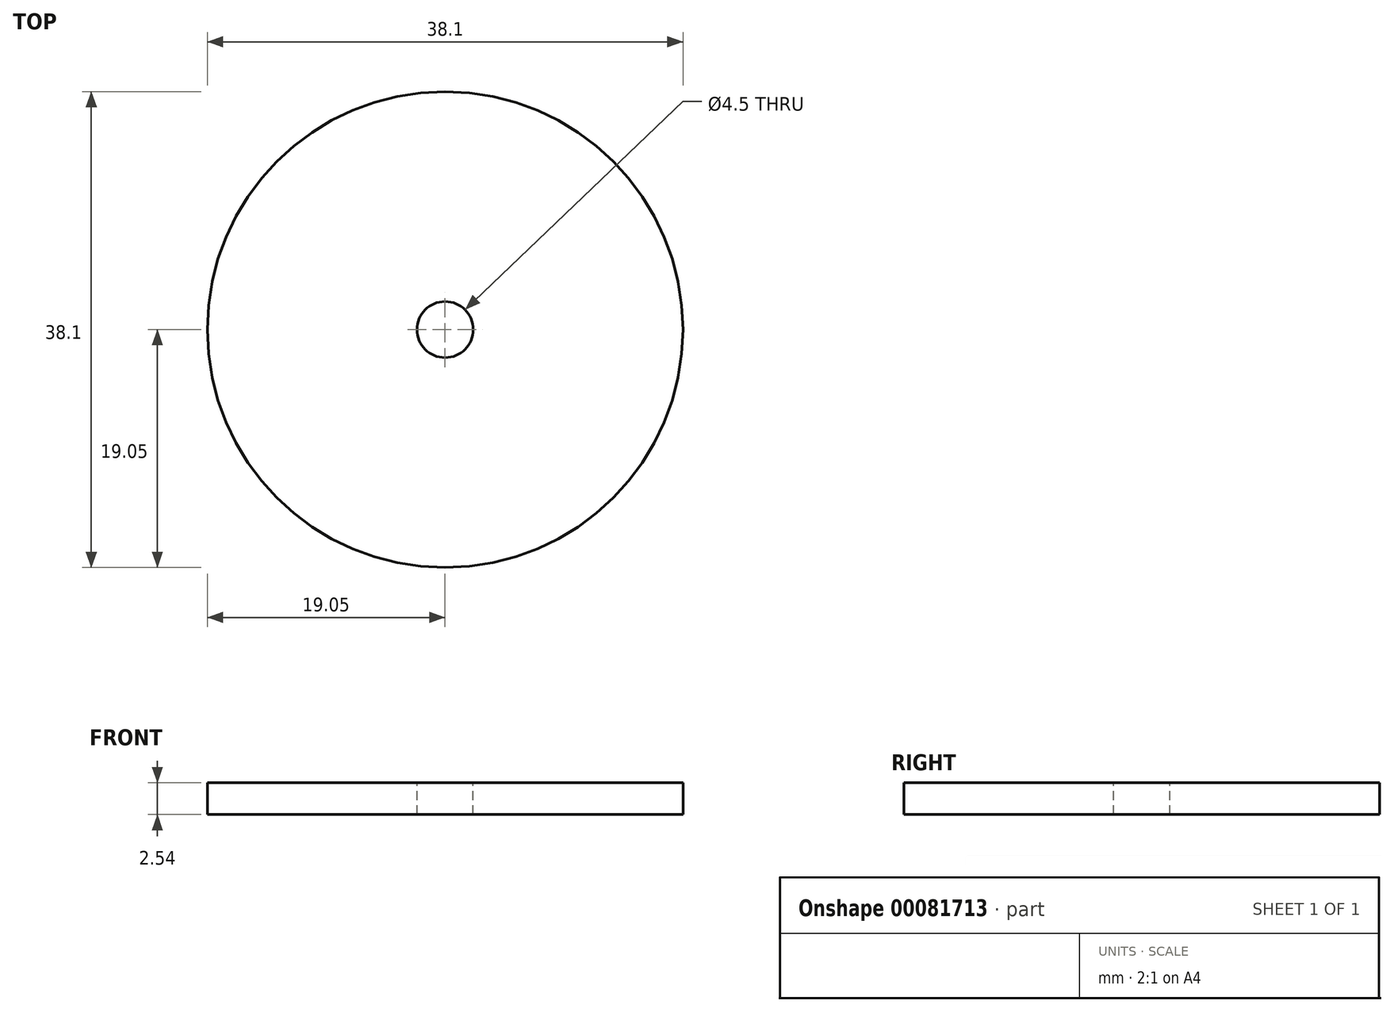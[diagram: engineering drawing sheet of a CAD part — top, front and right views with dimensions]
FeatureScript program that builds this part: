
annotation { "Feature Type Name" : "Feature", "Feature Type Description" : "" }
export const myFeature = defineFeature(function(context is Context, id is Id, definition is map)
    precondition{}
    {
        {
            var Q0;
            Q0=qCreatedBy(makeId("Top.planeOp"),FACE);
            var sketch = newSketch(context, id + "F0", { "sketchPlane" : qUnion([Q0])});
            skCircle(sketch, "E0", {"center": v(0, 0) * mm, "radius": 19.05 * mm});
            skSolve(sketch);
        }
        {
            var Q0;
            Q0 = qSketchRegion(id + "F0", true);
            extrude(context, id + "F1", {"entities" : qUnion([Q0]), "depth" : 2.54 * mm});
        }
        {
            var Q0;
            Q0=makeQuery(id+"F1.opExtrude","CAP_FACE",FACE,{"disambiguationData":[OSD([sQuery(id+"F0.wireOp",EDGE,"E0")])],"isStart":false});
            var sketch = newSketch(context, id + "F2", { "sketchPlane" : qUnion([Q0])});
            skPoint(sketch, "E1", {"position": v(0, 0) * mm});
            skSolve(sketch);
        }
        {
            var Q0;
            Q0=sQuery(id+"F2.wireOp",VERTEX,"E1");
            var Q1;
            Q1=makeQuery(id+"F1.opExtrude","SWEPT_BODY",BODY,{"disambiguationData":[OSD([sQuery(id+"F0.wireOp",EDGE,"E0")])]});
            hole(context, id + "F3", {"style" : HoleStyle.SIMPLE, "endStyle" : HoleEndStyle.THROUGH, "standardTappedOrClearance" : lookupTablePath({ "standard" : "ANSI", "fit" : "Normal (ASME)", "size" : "#8", "type" : "Clearance" }), "standardBlindInLast" : lookupTablePath({ "fit" : "Free", "standard" : "ANSI", "size" : "#8", "type" : "Clearance" }), "holeDiameter" : 4.5 * mm, "startFromSketch" : true, "locations" : qUnion([Q0]), "scope" : qUnion([Q1]), "isTappedThrough" : true});
        }
    });
